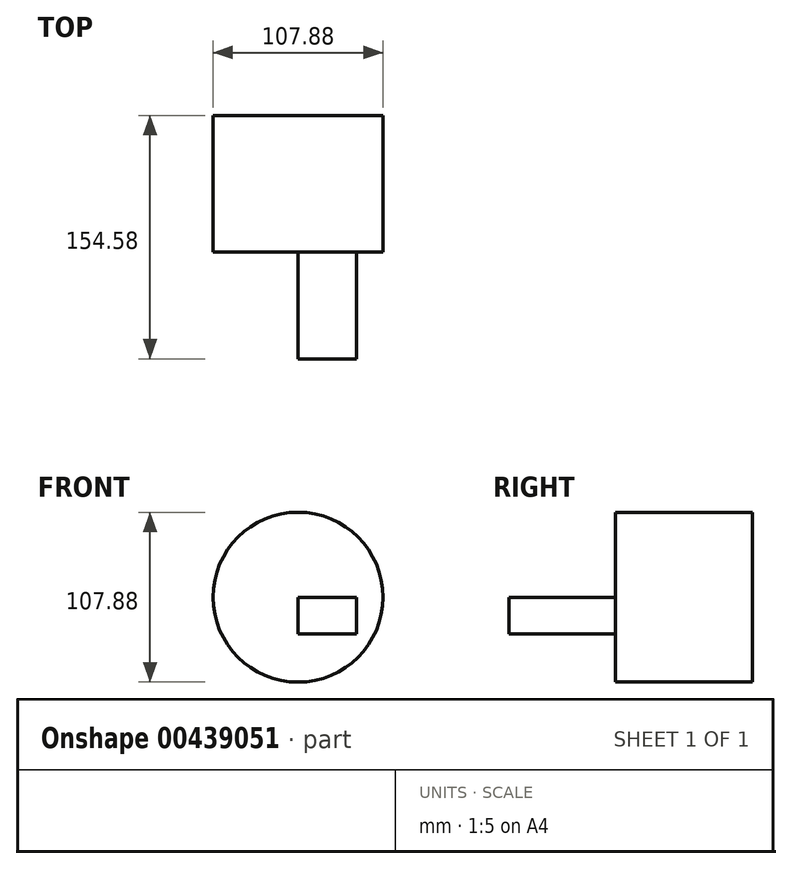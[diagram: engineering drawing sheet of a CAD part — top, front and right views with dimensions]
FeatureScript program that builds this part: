
annotation { "Feature Type Name" : "Feature", "Feature Type Description" : "" }
export const myFeature = defineFeature(function(context is Context, id is Id, definition is map)
    precondition{}
    {
        {
            var Q0;
            Q0=qCreatedBy(makeId("Front.planeOp"),FACE);
            var sketch = newSketch(context, id + "F0", { "sketchPlane" : qUnion([Q0])});
            skCircle(sketch, "E0", {"center": v(0, 0) * mm, "radius": 53.94 * mm});
            skSolve(sketch);
        }
        {
            var Q0;
            Q0=makeQuery(id+"F0.imprint","IMPRINT",FACE,{"disambiguationData":[TD([[makeQuery(id+"F0.imprint","IMPRINT",EDGE,{"derivedFrom":sQuery(id+"F0.wireOp",EDGE,"E0")}),1.0]])]});
            extrude(context, id + "F1", {"entities" : qUnion([Q0]), "depth" : 86.9 * mm});
        }
        {
            var Q0;
            Q0=makeQuery(id+"F1.opExtrude","CAP_FACE",FACE,{"disambiguationData":[OSD([sQuery(id+"F0.wireOp",EDGE,"E0")])],"isStart":false});
            var sketch = newSketch(context, id + "F2", { "sketchPlane" : qUnion([Q0])});
            skLineSegment(sketch, "E1.bottom", {"start": v(0, 0) * mm, "end": v(0, 0) * mm});
            skLineSegment(sketch, "E1.top", {"start": v(0, -23.46) * mm, "end": v(0, -23.46) * mm});
            skLineSegment(sketch, "E1.left", {"start": v(0, 0) * mm, "end": v(0, -23.46) * mm});
            skLineSegment(sketch, "E1.right", {"start": v(0, 0) * mm, "end": v(0, -23.46) * mm});
            skLineSegment(sketch, "E2.bottom", {"start": v(36.98, 0) * mm, "end": v(0, 0) * mm});
            skLineSegment(sketch, "E2.top", {"start": v(36.98, -23.46) * mm, "end": v(0, -23.46) * mm});
            skLineSegment(sketch, "E2.left", {"start": v(36.98, 0) * mm, "end": v(36.98, -23.46) * mm});
            skSolve(sketch);
        }
        {
            var Q0;
            Q0=makeQuery(id+"F2.imprint","IMPRINT",FACE,{"disambiguationData":[TD([[makeQuery(id+"F2.imprint","IMPRINT",EDGE,{"derivedFrom":sQuery(id+"F2.wireOp",EDGE,"E2.bottom")}),1.0]])]});
            extrude(context, id + "F3", {"entities" : qUnion([Q0]), "operationType" : NewBodyOperationType.ADD, "depth" : 67.69 * mm});
        }
    });
